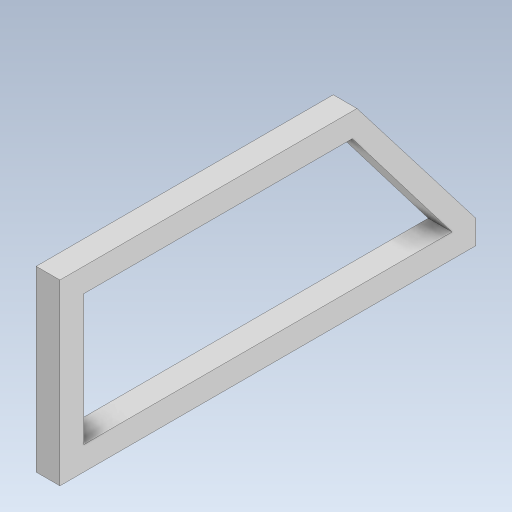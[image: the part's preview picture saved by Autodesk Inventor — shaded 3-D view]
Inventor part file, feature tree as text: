
AUTODESK INVENTOR PART (.ipt)
format: ipt  version: 2023.5 (Build 275446000, 446)  size: 261,632 bytes
history: native  units: in
note: dims shown in document units (in); Inventor stores cm internally (conversion verified against a paired STEP export)
features: extrude x1, sketch x1
ambient origin geometry x8: Origin, YZ Plane, XZ Plane, XY Plane, X Axis, Y Axis, Z Axis, Center Point
bodies: Solid1 (feature_tree)
feature tree (2):
  extrude  "Extrusion1"  Depth=2.7559in
  sketch  "Sketch1"  dims[d0=0.1575in d1=2.7559in d2=1.1811in d3=0.1575in d4=0.1575in d5=1.9685in d6=0.1575in d7=0.1575in d8=0.0in]
